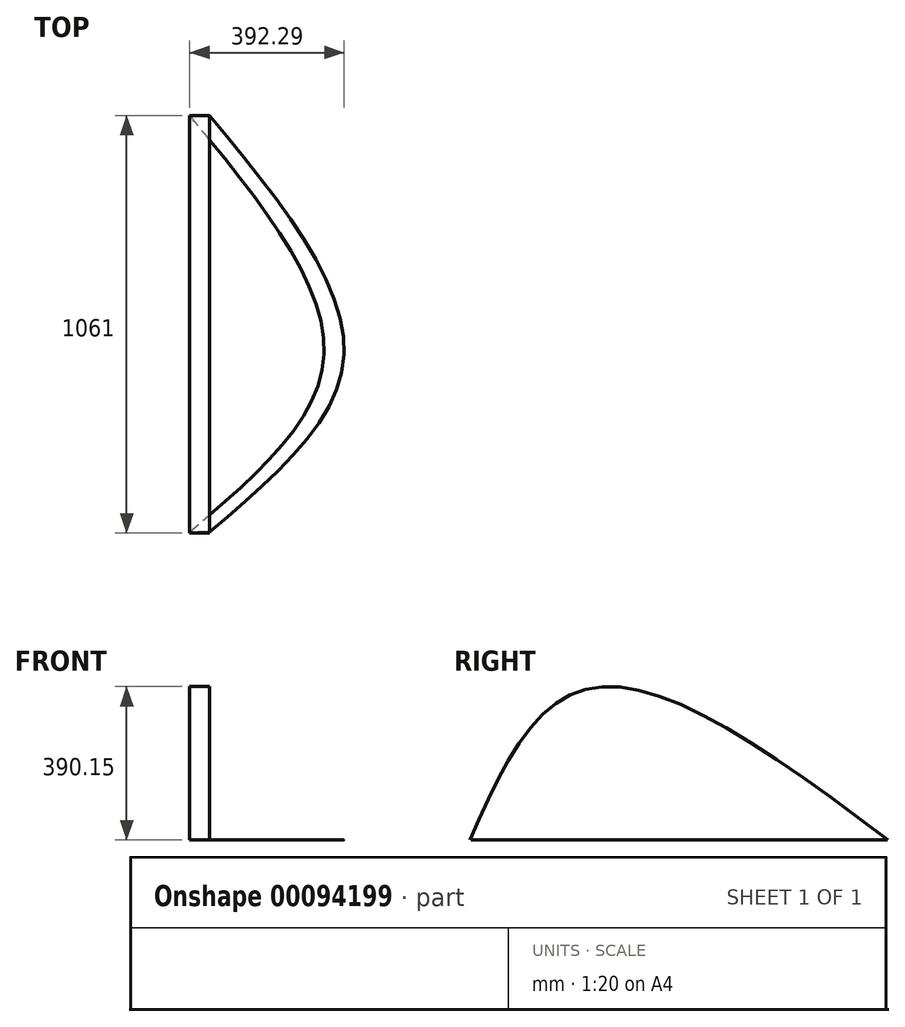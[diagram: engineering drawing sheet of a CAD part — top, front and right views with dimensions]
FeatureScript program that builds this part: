
annotation { "Feature Type Name" : "Feature", "Feature Type Description" : "" }
export const myFeature = defineFeature(function(context is Context, id is Id, definition is map)
    precondition{}
    {
        {
            var Q0;
            Q0=qCreatedBy(makeId("Right.planeOp"),FACE);
            var sketch = newSketch(context, id + "F0", { "sketchPlane" : qUnion([Q0])});
            skLineSegment(sketch, "E0", {"start": v(-265.25, 0) * mm, "end": v(795.75, 0) * mm});
            skLineSegment(sketch, "E1", {"start": v(-161.22, 381) * mm, "end": v(263.61, 381) * mm});
            skLineSegment(sketch, "E2", {"start": v(263.61, 381) * mm, "end": v(796.14, 309) * mm});
            skFitSpline(sketch, "E3", {"points": [v(-265.25, 0) * mm, v(19.76, 381) * mm, v(795.75, 0) * mm], "startDerivative": vector(523.84, 1226.38) * mm, "endDerivative": vector(1723.34, -1319.52) * mm});
            skSolve(sketch);
        }
        {
            var Q0;
            Q0=qCreatedBy(makeId("Top.planeOp"),FACE);
            var sketch = newSketch(context, id + "F1", { "sketchPlane" : qUnion([Q0])});
            skFitSpline(sketch, "E4", {"points": [v(0, -262.62) * mm, v(340.73, 180.45) * mm, v(0, 795.4) * mm], "startDerivative": vector(1045.14, 887.36) * mm, "endDerivative": vector(-1005.98, 1222.29) * mm});
            skSolve(sketch);
        }
        {
            var Q0;
            Q0=sQuery(id+"F0.wireOp",EDGE,"E3");
            var Q1;
            Q1=sQuery(id+"F1.wireOp",EDGE,"E4");
            extrude(context, id + "F2", {"bodyType" : ToolBodyType.SURFACE, "surfaceEntities" : qUnion([Q0, Q1]), "oppositeDirection" : true, "depth" : 50.8 * mm});
        }
    });
